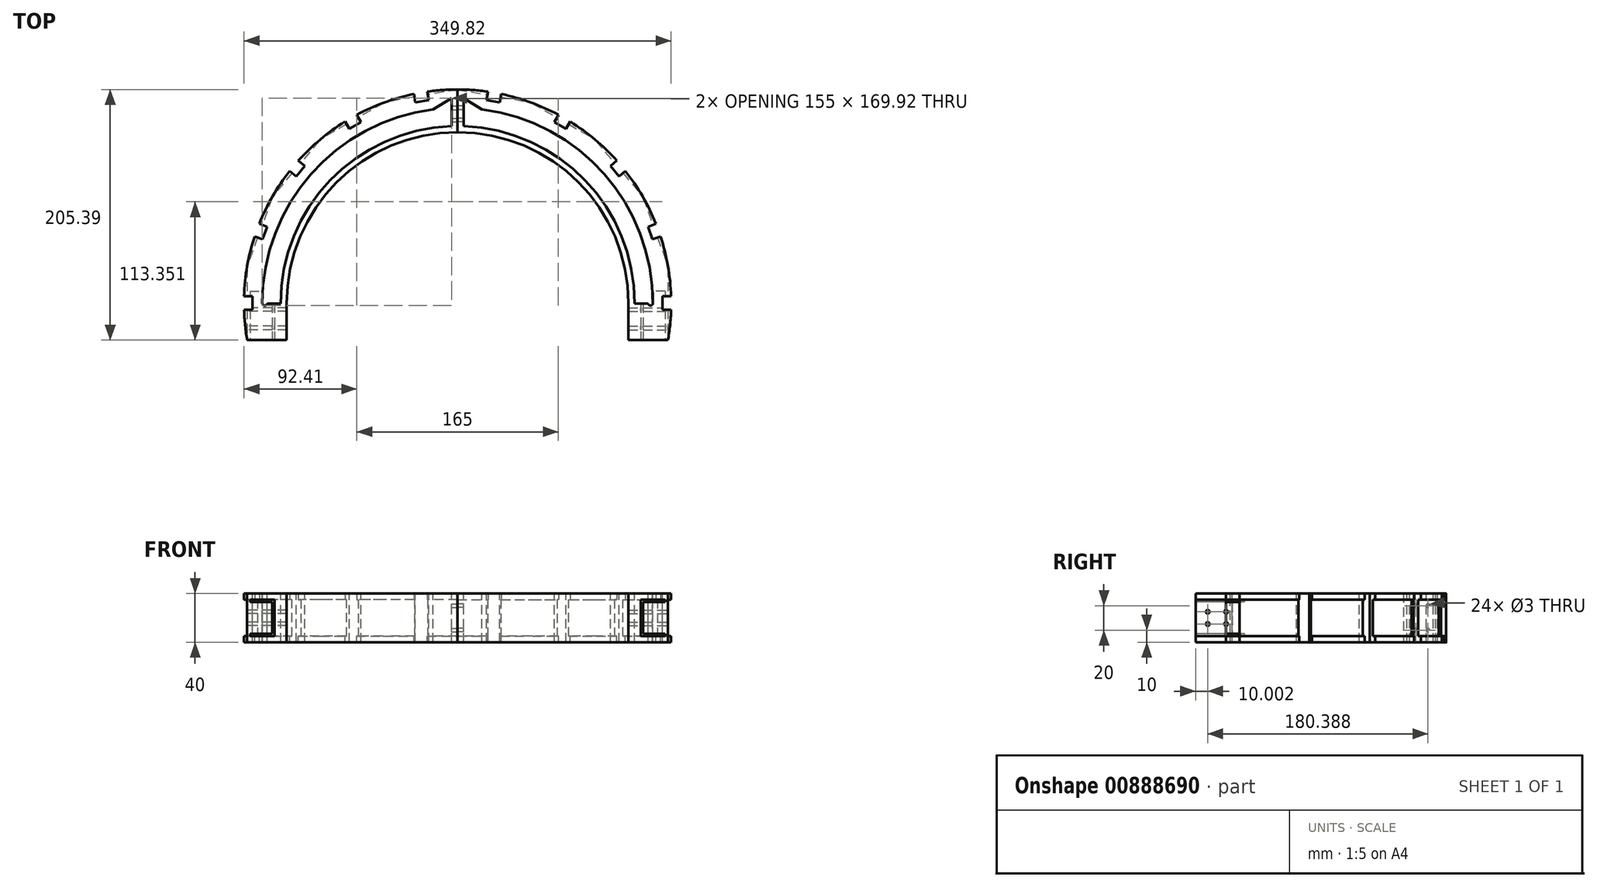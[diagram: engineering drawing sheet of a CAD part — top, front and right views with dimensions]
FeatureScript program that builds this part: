
annotation { "Feature Type Name" : "Feature", "Feature Type Description" : "" }
export const myFeature = defineFeature(function(context is Context, id is Id, definition is map)
    precondition{}
    {
        {
            var Q0;
            Q0=qCreatedBy(makeId("Top.planeOp"),FACE);
            var sketch = newSketch(context, id + "F0", { "sketchPlane" : qUnion([Q0])});
            skCircle(sketch, "E0", {"center": v(0, 0) * mm, "radius": 175 * mm, "construction": true});
            skCircle(sketch, "E1", {"center": v(0, 0) * mm, "radius": 140 * mm, "construction": true});
            skLineSegment(sketch, "E2", {"start": v(0, 0) * mm, "end": v(-230.33, 83.83) * mm, "construction": true});
            skLineSegment(sketch, "E3", {"start": v(0, 0) * mm, "end": v(-174.26, 146.22) * mm, "construction": true});
            skLineSegment(sketch, "E4", {"start": v(0, 0) * mm, "end": v(-109.36, 189.42) * mm, "construction": true});
            skLineSegment(sketch, "E5", {"start": v(0, 0) * mm, "end": v(-37.45, 212.42) * mm, "construction": true});
            skLineSegment(sketch, "E6", {"start": v(-172.34, 30.39) * mm, "end": v(-172.34, -30.39) * mm});
            skLineSegment(sketch, "E7", {"start": v(-172.34, -30.39) * mm, "end": v(-140, -30.39) * mm});
            skLineSegment(sketch, "E8", {"start": v(0, -30.39) * mm, "end": v(0, 0) * mm});
            skLineSegment(sketch, "E9", {"start": v(0, 175) * mm, "end": v(-59.85, 164.45) * mm});
            skLineSegment(sketch, "E10", {"start": v(-59.85, 164.45) * mm, "end": v(-112.49, 134.06) * mm});
            skLineSegment(sketch, "E11", {"start": v(-112.49, 134.06) * mm, "end": v(-151.55, 87.5) * mm});
            skLineSegment(sketch, "E12", {"start": v(-151.55, 87.5) * mm, "end": v(-172.34, 30.39) * mm});
            skLineSegment(sketch, "E13", {"start": v(0, 0) * mm, "end": v(-233.04, 0) * mm, "construction": true});
            skPoint(sketch, "E13.endSnap0", {"position": v(-172.34, 0) * mm});
            skArc(sketch, "E14", {"start": v(-140, 0) * mm, "mid": v(-99, 99) * mm, "end": v(0, 140) * mm});
            skLineSegment(sketch, "E15", {"start": v(-140, 0) * mm, "end": v(-140, -30.39) * mm});
            skLineSegment(sketch, "E16.trimOffspring", {"start": v(0, 140) * mm, "end": v(0, 175) * mm});
            skCircle(sketch, "E17", {"center": v(0, 0) * mm, "radius": 150 * mm, "construction": true});
            skSolve(sketch);
        }
        {
            var Q0;
            Q0 = qSketchRegion(id + "F0", true);
            extrude(context, id + "F1", {"entities" : qUnion([Q0]), "depth" : 30 * mm, "offsetDistance" : 25 * mm});
        }
        {
            var Q0;
            Q0=makeQuery(id+"F1.opExtrude","CAP_FACE",FACE,{"disambiguationData":[OSD([sQuery(id+"F0.wireOp",EDGE,"E6"),sQuery(id+"F0.wireOp",EDGE,"E7"),sQuery(id+"F0.wireOp",EDGE,"E9"),sQuery(id+"F0.wireOp",EDGE,"E10"),sQuery(id+"F0.wireOp",EDGE,"E11"),sQuery(id+"F0.wireOp",EDGE,"E12"),sQuery(id+"F0.wireOp",EDGE,"E14"),sQuery(id+"F0.wireOp",EDGE,"E15"),sQuery(id+"F0.wireOp",EDGE,"E16.trimOffspring")])],"isStart":false});
            var sketch = newSketch(context, id + "F2", { "sketchPlane" : qUnion([Q0])});
            skArc(sketch, "E18", {"start": v(0, 175) * mm, "mid": v(-134.06, 112.49) * mm, "end": v(-172.34, -30.39) * mm});
            skArc(sketch, "E19", {"start": v(0, 140) * mm, "mid": v(-99, 99) * mm, "end": v(-140, 0) * mm});
            skLineSegment(sketch, "E20", {"start": v(-140, 0) * mm, "end": v(-140, -30.39) * mm});
            skLineSegment(sketch, "E21", {"start": v(-140, -30.39) * mm, "end": v(-172.34, -30.39) * mm});
            skLineSegment(sketch, "E22", {"start": v(0, 175) * mm, "end": v(0, 140) * mm});
            skSolve(sketch);
        }
        {
            var Q0;
            Q0 = qSketchRegion(id + "F2", true);
            extrude(context, id + "F3", {"entities" : qUnion([Q0]), "operationType" : NewBodyOperationType.ADD, "depth" : 5 * mm, "offsetDistance" : 25 * mm});
        }
        {
            var Q0;
            Q0=makeQuery(id+"F1.opExtrude","CAP_FACE",FACE,{"disambiguationData":[OSD([sQuery(id+"F0.wireOp",EDGE,"E6"),sQuery(id+"F0.wireOp",EDGE,"E7"),sQuery(id+"F0.wireOp",EDGE,"E9"),sQuery(id+"F0.wireOp",EDGE,"E10"),sQuery(id+"F0.wireOp",EDGE,"E11"),sQuery(id+"F0.wireOp",EDGE,"E12"),sQuery(id+"F0.wireOp",EDGE,"E14"),sQuery(id+"F0.wireOp",EDGE,"E15"),sQuery(id+"F0.wireOp",EDGE,"E16.trimOffspring")])],"isStart":true});
            var sketch = newSketch(context, id + "F4", { "sketchPlane" : qUnion([Q0])});
            skArc(sketch, "E23", {"start": v(0, -175) * mm, "mid": v(-134.06, -112.49) * mm, "end": v(-172.34, 30.39) * mm});
            skArc(sketch, "E24", {"start": v(0, -140) * mm, "mid": v(-99, -99) * mm, "end": v(-140, 0) * mm});
            skLineSegment(sketch, "E25", {"start": v(-172.34, 30.39) * mm, "end": v(-140, 30.39) * mm});
            skLineSegment(sketch, "E26", {"start": v(-140, 30.39) * mm, "end": v(-140, 0) * mm});
            skLineSegment(sketch, "E27", {"start": v(0, -140) * mm, "end": v(0, -175) * mm});
            skSolve(sketch);
        }
        {
            var Q0;
            Q0 = qSketchRegion(id + "F4", true);
            extrude(context, id + "F5", {"entities" : qUnion([Q0]), "operationType" : NewBodyOperationType.ADD, "depth" : 5 * mm, "offsetDistance" : 25 * mm});
        }
        {
            var Q0;
            Q0=makeQuery(id+"F5.boolean.opBoolean","MERGE",FACE,{"derivedFrom":[makeQuery(id+"F3.boolean.opBoolean","MERGE",FACE,{"derivedFrom":[makeQuery(id+"F1.opExtrude","SWEPT_FACE",FACE,{"disambiguationData":[OSD([sQuery(id+"F0.wireOp",EDGE,"E7")])]}),makeQuery(id+"F3.opExtrude","SWEPT_FACE",FACE,{"disambiguationData":[OSD([sQuery(id+"F2.wireOp",EDGE,"E21")])]})]}),makeQuery(id+"F5.opExtrude","SWEPT_FACE",FACE,{"disambiguationData":[OSD([sQuery(id+"F4.wireOp",EDGE,"E25")])]})]});
            var sketch = newSketch(context, id + "F6", { "sketchPlane" : qUnion([Q0])});
            skLineSegment(sketch, "E28", {"start": v(-150, 58.64) * mm, "end": v(-150, -22.11) * mm, "construction": true});
            skLineSegment(sketch, "E29", {"start": v(-150, 0) * mm, "end": v(-170, 0) * mm});
            skLineSegment(sketch, "E30", {"start": v(-170, 0) * mm, "end": v(-170, 2) * mm});
            skLineSegment(sketch, "E31", {"start": v(-170, 2) * mm, "end": v(-152, 2) * mm});
            skLineSegment(sketch, "E32", {"start": v(-152, 2) * mm, "end": v(-152, 28) * mm});
            skLineSegment(sketch, "E33", {"start": v(-150, 30) * mm, "end": v(-150, 0) * mm});
            skLineSegment(sketch, "E34", {"start": v(-170, 28) * mm, "end": v(-152, 28) * mm});
            skLineSegment(sketch, "E35", {"start": v(-170, 28) * mm, "end": v(-170, 30) * mm});
            skLineSegment(sketch, "E36", {"start": v(-170, 30) * mm, "end": v(-150, 30) * mm});
            skSolve(sketch);
        }
        {
            var Q0;
            Q0 = qSketchRegion(id + "F6", true);
            extrude(context, id + "F7", {"entities" : qUnion([Q0]), "operationType" : NewBodyOperationType.REMOVE, "oppositeDirection" : true, "depth" : 40 * mm, "offsetDistance" : 25 * mm});
        }
        {
            var Q0;
            Q0=makeQuery(id+"F1.opExtrude","SWEPT_FACE",FACE,{"disambiguationData":[OSD([sQuery(id+"F0.wireOp",EDGE,"E6")])]});
            var sketch = newSketch(context, id + "F8", { "sketchPlane" : qUnion([Q0])});
            skPoint(sketch, "E37", {"position": v(30.39, 15) * mm});
            skCircle(sketch, "E38", {"center": v(20.39, 20) * mm, "radius": 1.5 * mm});
            skLineSegment(sketch, "E39", {"start": v(30.39, 15) * mm, "end": v(-8.33, 15) * mm, "construction": true});
            skCircle(sketch, "E40.MirrorC", {"center": v(20.39, 10) * mm, "radius": 1.5 * mm});
            skCircle(sketch, "E41", {"center": v(5.39, 20) * mm, "radius": 1.5 * mm});
            skCircle(sketch, "E42.MirrorC", {"center": v(5.39, 10) * mm, "radius": 1.5 * mm});
            skSolve(sketch);
        }
        {
            var Q0;
            Q0 = qSketchRegion(id + "F8", true);
            extrude(context, id + "F9", {"entities" : qUnion([Q0]), "operationType" : NewBodyOperationType.REMOVE, "endBound" : BoundingType.THROUGH_ALL, "oppositeDirection" : true, "depth" : 25 * mm, "offsetDistance" : 25 * mm});
        }
        {
            var Q0;
            Q0=makeQuery(id+"F3.opExtrude","CAP_FACE",FACE,{"disambiguationData":[OSD([sQuery(id+"F2.wireOp",EDGE,"E18"),sQuery(id+"F2.wireOp",EDGE,"E19"),sQuery(id+"F2.wireOp",EDGE,"E20"),sQuery(id+"F2.wireOp",EDGE,"E21"),sQuery(id+"F2.wireOp",EDGE,"E22")])],"isStart":false});
            var sketch = newSketch(context, id + "F10", { "sketchPlane" : qUnion([Q0])});
            skLineSegment(sketch, "E43", {"start": v(-5, 144.91) * mm, "end": v(-5, 159.92) * mm});
            skLineSegment(sketch, "E44", {"start": v(0, 0) * mm, "end": v(-34.58, 196.13) * mm, "construction": true});
            skLineSegment(sketch, "E45", {"start": v(0, 0) * mm, "end": v(-103.7, 179.6) * mm, "construction": true});
            skLineSegment(sketch, "E46", {"start": v(0, 0) * mm, "end": v(-161.52, 135.53) * mm, "construction": true});
            skLineSegment(sketch, "E47", {"start": v(0, 0) * mm, "end": v(-196.3, 71.45) * mm, "construction": true});
            skLineSegment(sketch, "E48", {"start": v(0, 0) * mm, "end": v(-211.35, 0) * mm, "construction": true});
            skLineSegment(sketch, "E49", {"start": v(-24.97, 173.3) * mm, "end": v(-23.76, 166.4) * mm});
            skLineSegment(sketch, "E50", {"start": v(-23.76, 166.4) * mm, "end": v(-34.59, 164.5) * mm});
            skLineSegment(sketch, "E51", {"start": v(-24.97, 173.3) * mm, "end": v(-35.8, 171.39) * mm});
            skLineSegment(sketch, "E52", {"start": v(-35.8, 171.39) * mm, "end": v(-34.59, 164.5) * mm});
            skLineSegment(sketch, "E53", {"start": v(-92.26, 148.8) * mm, "end": v(-82.74, 154.3) * mm});
            skLineSegment(sketch, "E54", {"start": v(-82.74, 154.3) * mm, "end": v(-79.24, 148.24) * mm});
            skLineSegment(sketch, "E55", {"start": v(-79.24, 148.24) * mm, "end": v(-88.76, 142.74) * mm});
            skLineSegment(sketch, "E56", {"start": v(-88.76, 142.74) * mm, "end": v(-92.26, 148.8) * mm});
            skLineSegment(sketch, "E57", {"start": v(-137.6, 108.27) * mm, "end": v(-130.52, 116.7) * mm});
            skLineSegment(sketch, "E58", {"start": v(-130.52, 116.7) * mm, "end": v(-125.16, 112.2) * mm});
            skLineSegment(sketch, "E59", {"start": v(-125.16, 112.2) * mm, "end": v(-132.23, 103.78) * mm});
            skLineSegment(sketch, "E60", {"start": v(-132.23, 103.78) * mm, "end": v(-137.6, 108.27) * mm});
            skLineSegment(sketch, "E61", {"start": v(-162.57, 65.02) * mm, "end": v(-166.33, 54.69) * mm});
            skLineSegment(sketch, "E62", {"start": v(-166.33, 54.69) * mm, "end": v(-159.75, 52.3) * mm});
            skLineSegment(sketch, "E63", {"start": v(-159.75, 52.3) * mm, "end": v(-155.99, 62.63) * mm});
            skLineSegment(sketch, "E64", {"start": v(-155.99, 62.63) * mm, "end": v(-162.57, 65.02) * mm});
            skLineSegment(sketch, "E65", {"start": v(-175, 5.5) * mm, "end": v(-175, -5.5) * mm});
            skLineSegment(sketch, "E66", {"start": v(-175, -5.5) * mm, "end": v(-168, -5.5) * mm});
            skLineSegment(sketch, "E67", {"start": v(-168, -5.5) * mm, "end": v(-168, 5.5) * mm});
            skLineSegment(sketch, "E68", {"start": v(-168, 5.5) * mm, "end": v(-175, 5.5) * mm});
            skCircle(sketch, "E69", {"center": v(-79, 136.83) * mm, "radius": 2 * mm});
            skCircle(sketch, "E70", {"center": v(-121.04, 101.56) * mm, "radius": 2 * mm});
            skCircle(sketch, "E71", {"center": v(-148.47, 54.04) * mm, "radius": 2 * mm});
            skCircle(sketch, "E72", {"center": v(-158, 0) * mm, "radius": 2 * mm});
            skArc(sketch, "E73", {"start": v(-20, 158.75) * mm, "mid": v(-120.13, 105.68) * mm, "end": v(-160, -0.39) * mm});
            skArc(sketch, "E74", {"start": v(-5, 144.91) * mm, "mid": v(-104.42, 100.6) * mm, "end": v(-145, -0.39) * mm});
            skLineSegment(sketch, "E75", {"start": v(-160, -0.39) * mm, "end": v(-145, -0.39) * mm});
            skLineSegment(sketch, "E76", {"start": v(-20, 158.75) * mm, "end": v(-5, 167.92) * mm});
            skLineSegment(sketch, "E77", {"start": v(-5, 167.92) * mm, "end": v(-5, 159.92) * mm});
            skSolve(sketch);
        }
        {
            var Q0;
            Q0 = qSketchRegion(id + "F10", true);
            extrude(context, id + "F11", {"entities" : qUnion([Q0]), "operationType" : NewBodyOperationType.REMOVE, "endBound" : BoundingType.THROUGH_ALL, "oppositeDirection" : true, "depth" : 25 * mm, "offsetDistance" : 25 * mm});
        }
        {
            var Q0;
            Q0=makeQuery(id+"F5.boolean.opBoolean","MERGE",FACE,{"derivedFrom":[makeQuery(id+"F3.boolean.opBoolean","MERGE",FACE,{"derivedFrom":[makeQuery(id+"F1.opExtrude","SWEPT_FACE",FACE,{"disambiguationData":[OSD([sQuery(id+"F0.wireOp",EDGE,"E16.trimOffspring")])]}),makeQuery(id+"F3.opExtrude","SWEPT_FACE",FACE,{"disambiguationData":[OSD([sQuery(id+"F2.wireOp",EDGE,"E22")])]})]}),makeQuery(id+"F5.opExtrude","SWEPT_FACE",FACE,{"disambiguationData":[OSD([sQuery(id+"F4.wireOp",EDGE,"E27")])]})]});
            var sketch = newSketch(context, id + "F12", { "sketchPlane" : qUnion([Q0])});
            skLineSegment(sketch, "E78", {"start": v(140, 15) * mm, "end": v(175, 15) * mm, "construction": true});
            skCircle(sketch, "E79", {"center": v(150, 25) * mm, "radius": 1.5 * mm});
            skCircle(sketch, "E80", {"center": v(160, 25) * mm, "radius": 1.5 * mm});
            skCircle(sketch, "E81.MirrorC", {"center": v(150, 5) * mm, "radius": 1.5 * mm});
            skCircle(sketch, "E82.MirrorC", {"center": v(160, 5) * mm, "radius": 1.5 * mm});
            skSolve(sketch);
        }
        {
            var Q0;
            Q0 = qSketchRegion(id + "F12", true);
            extrude(context, id + "F13", {"entities" : qUnion([Q0]), "operationType" : NewBodyOperationType.REMOVE, "oppositeDirection" : true, "depth" : 10 * mm, "offsetDistance" : 25 * mm});
        }
        {
            var Q0;
            Q0=makeQuery(id+"F1.opExtrude","SWEPT_EDGE",EDGE,{"disambiguationData":[OSD([sQuery(id+"F0.wireOp",EDGE,"E9"),sQuery(id+"F0.wireOp",EDGE,"E10")])]});
            var Q1;
            Q1=makeQuery(id+"F1.opExtrude","SWEPT_EDGE",EDGE,{"disambiguationData":[OSD([sQuery(id+"F0.wireOp",EDGE,"E10"),sQuery(id+"F0.wireOp",EDGE,"E11")])]});
            var Q2;
            Q2=makeQuery(id+"F1.opExtrude","SWEPT_EDGE",EDGE,{"disambiguationData":[OSD([sQuery(id+"F0.wireOp",EDGE,"E11"),sQuery(id+"F0.wireOp",EDGE,"E12")])]});
            var Q3;
            Q3=makeQuery(id+"F1.opExtrude","SWEPT_EDGE",EDGE,{"disambiguationData":[OSD([sQuery(id+"F0.wireOp",EDGE,"E6"),sQuery(id+"F0.wireOp",EDGE,"E12")])]});
            fillet(context, id + "F14", {"entities" : qUnion([Q0, Q1, Q2, Q3]), "radius" : 10 * mm, "tangentPropagation" : true, "allowEdgeOverflow" : false});
        }
        {
            var Q0;
            Q0=makeQuery(id+"F1.opExtrude","SWEPT_BODY",BODY,{"disambiguationData":[OSD([sQuery(id+"F0.wireOp",EDGE,"E6"),sQuery(id+"F0.wireOp",EDGE,"E7"),sQuery(id+"F0.wireOp",EDGE,"E9"),sQuery(id+"F0.wireOp",EDGE,"E10"),sQuery(id+"F0.wireOp",EDGE,"E11"),sQuery(id+"F0.wireOp",EDGE,"E12"),sQuery(id+"F0.wireOp",EDGE,"E14"),sQuery(id+"F0.wireOp",EDGE,"E15"),sQuery(id+"F0.wireOp",EDGE,"E16.trimOffspring")])]});
            var Q1;
            Q1=qCreatedBy(makeId("Right.planeOp"),FACE);
            mirror(context, id + "F15", {"entities" : qUnion([Q0]), "mirrorPlane" : qUnion([Q1])});
        }
    });
